# Revit family: Flooring_Entrance-Flooring_emco_DIPLOMAT-Original
name_source: partatom
category: Furniture Systems
revit_build: Autodesk Revit 2018 (Build: 20190510_1515(x64)
units: mm (PartAtom-declared; Revit-internal decimal feet)

## family parameters
Cut with Voids When Loaded = No
Host = Face
OmniClass Number = 23.15.17.11.11
OmniClass Title = Floor Toppings
Part Type = Normal
Room Calculation Point = No
Round Connector Dimension = Use Diameter
Shared = No

## types (1)
- Default - please load Revit Family Type Catalog
    Assembly Code = E2010400
    Brush strip = No
    Cassette brush = No
    Colour fastness to artificial light ISO 105-B02 = good 6
    Colour fastness to rubbing ISO 105 X12 = good 4
    Colour fastness to water ISO 105 E01 = good 5
    Date Updated = 2023/08/22
    Default Elevation = 1219 mm
    Description = Rollable and hard-wearing original entrance mat with standard insert for supported installation options.
    EPIMID = 99817
    Flammability = Insert for Light Grey and Anthracite ribbed carpet colours available on request (surcharge applicable) with fire classification Cfl-s1 according to EN 13501.
    Height 12 = Yes
    Height 17 = No
    Height 22 = No
    Keynote = 12480.A1
    Large = Yes
    Manufacturer = Emco
    Model = Large With ribbed carpet insert 512 LR
    Normal = No
    Pile material = 100% PP (polypropylene)
    Product data url = https://bimobject.com
    Profile Material = Emco - Metal - Aluminium
    Profile width (mm) = 44 mm
    Scraping edge = No
    Slip resistance = R 11 slip resistance as per DIN 51130
    Standard profile clearance approx. (mm) = 5 mm, rubber spacers
    Tread surface = Recessed, robust, weather-proof, ribbed carpet strips.
    URL = https://www.emco-bau.com
    Version = 1
    Weight (kg/m2) = 77
    z_Height = 12 mm  [stored 0.0393701 ft]
    z_edge_height = 16 mm
    z_insert_offset = 49 mm
    z_insert_width = 44 mm  [stored 0.144357 ft]
    z_slot_offest = 47 mm
    z_slot_width = 5 mm  [stored 0.0164042 ft]

note: [stored X ft] marks values corroborated as IEEE doubles in the binary element streams (Revit-internal decimal feet)

## geometry (parser evidence)
native form markers: Sweep x8
no freeform markers — native parametric forms only
